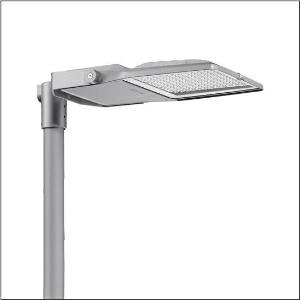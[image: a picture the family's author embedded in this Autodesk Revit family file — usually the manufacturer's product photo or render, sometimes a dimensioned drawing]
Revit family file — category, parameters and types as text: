
# Revit family: floodlight_fl_21_midi___pl61_5xa7785e2c3a_8e59
name_source: partatom
category: Lighting Fixtures
units: mm (PartAtom-declared; Revit-internal decimal feet)

## family parameters
Cut with Voids When Loaded = No
Host = Face
Light Source = No
Part Type = Normal
Room Calculation Point = No
Round Connector Dimension = Use Diameter
Shared = No

## types (1)
- --- (1 x LED, 26450 lm, 212.4 W, 3000K)
    Apparent Load = 212 VA
    CIE Flux Codes = 33 65 98 100 100
    Color Rendering = 70
    Color Temperature = 3000K
    Default Elevation = 1800 mm
    Description = Floodlight FL 21 midi, floodlight, primary light control with lens, of PMMA, primary optical cover: protective disc, of toughened safety glass, transparent, light distribution: PL61, light emission: direct distribution, installation type: surface-mounted, LED, High Power LED, rated luminous flux: 26.450lm, luminous efficacy: 125lm/W, light colour: 730, colour temperature: 3000K, control gear: ECG Smart Interface, control: flexible luminous flux parameterisation, time-dependent luminous flux control, constant luminous flux control, overheat protection, presetting dimming logarithmic, with terminal, 6-pole, mains connection: 220..240V, AC, 50/60Hz, start of lifetime: 212W, end of service life: 231W, reduction: 95W, luminaire housing, of diecast aluminium, powder-coated, Siteco® metallic grey (DB 702S), sealing non-destructively replaceable, please order mast flange separately, mast bracket, of steel, galvanised, powder-coated, Siteco® metallic grey (DB 702S), Smart Interface above, protection rating (complete): IP66, insulation class (complete): insulation class II (safety insulation), certification: CE, protection symbol: D, impact resistance: IK08, permissible operating ambient temperature: -20..+40°C, permissible operating ambient temperature for outdoor applications: -40..+50°C, standard: DIN EN 12944, LABS conformity tested according to VDMA 24364:2018-05, packaging unit: 1 piece

Light Distribution: PL61
    Height = 76 mm
    Lamp = 1 x LED
    Lamp Light Flux = 26450 lm
    Lamp Power = 212.4 W
    Lamp count = 1
    Length = 657 mm
    Luminous efficacy = 125 lm/W
    Manufacturer = Siteco
    ModVariant = No
    Model = 5XA7785E2C3A
    Number of Poles = 1
    OnlyDefault = Yes
    Power Factor = 1
    Product Name = Floodlight FL 21 midi | PL61
    Product group = floodlight | pylon annexe
    ProductGroupID = 6200
    Protection Class = Protection class II
    Protection Degree = IP 66
    RLX_Detail_Level = 1
    RLX_Emergency_Light_Flux = 0 lm
    RLX_Emergency_Type = 0
    RLX_Emergency_Type_DB = No
    RlxData = <blob elided: 153521 chars, md5=2f7af593>
    Socket = socket
    Standby Power = 0 W
    System Light Flux = 26450 lm
    System Power = 212 W
    Type Comments = factory setting: luminous flux: 100 % | dim-lin: 254 | 710 mA
    Type Image = l_1007123.jpg
    URL = http://relux.com
    VarID = @adj_146797
    Voltage = 0 V
    Weight = 0.00 kg
    Width = 442 mm

## geometry (parser evidence)
native form markers: Blend x4, Sweep x11
no freeform markers — native parametric forms only
